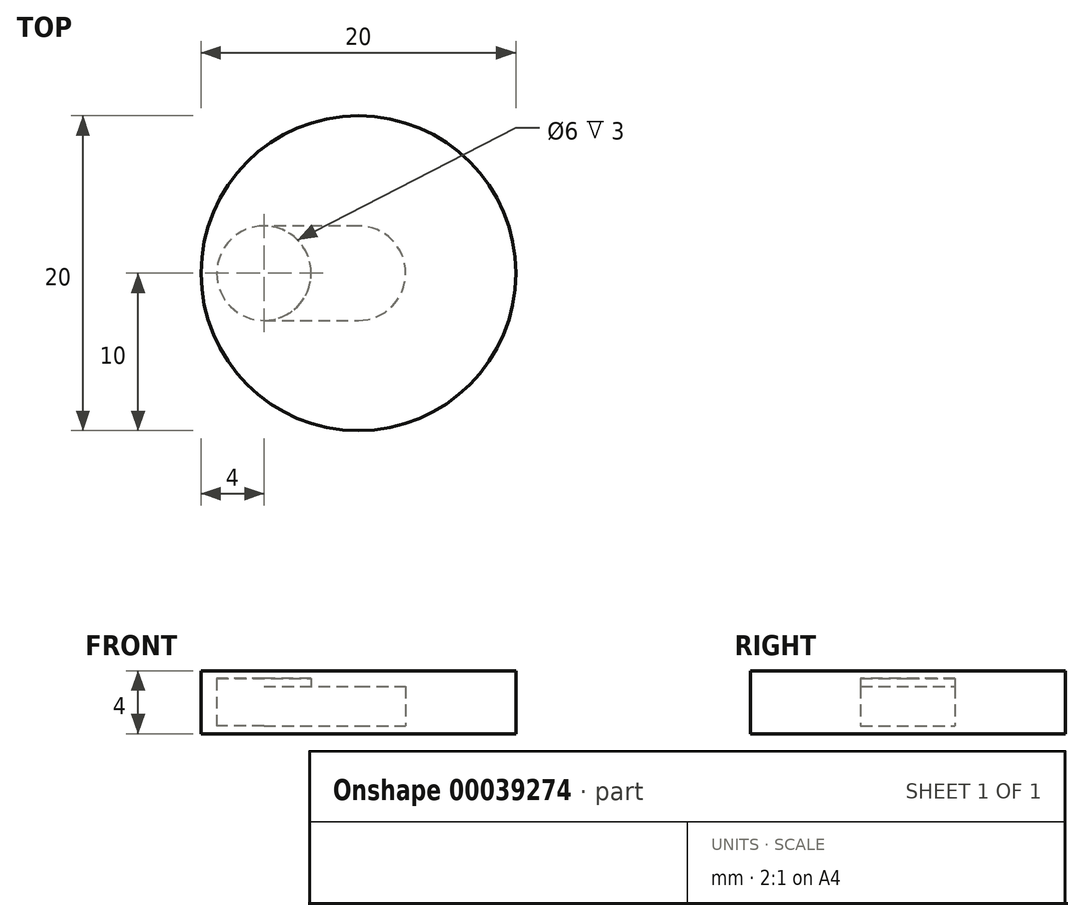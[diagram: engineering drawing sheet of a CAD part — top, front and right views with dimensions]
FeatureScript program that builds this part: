
annotation { "Feature Type Name" : "Feature", "Feature Type Description" : "" }
export const myFeature = defineFeature(function(context is Context, id is Id, definition is map)
    precondition{}
    {
        {
            var Q0;
            Q0=qCreatedBy(makeId("Top.planeOp"),FACE);
            var sketch = newSketch(context, id + "F0", { "sketchPlane" : qUnion([Q0])});
            skCircle(sketch, "E0", {"center": v(0, 0) * mm, "radius": 10 * mm});
            skCircle(sketch, "E1", {"center": v(0, 0) * mm, "radius": 3 * mm});
            skLineSegment(sketch, "E2", {"start": v(0, 0) * mm, "end": v(-6, 0) * mm, "construction": true});
            skCircle(sketch, "E3", {"center": v(-6, 0) * mm, "radius": 3 * mm});
            skLineSegment(sketch, "E4", {"start": v(-6, 0) * mm, "end": v(-6, 3) * mm, "construction": true});
            skLineSegment(sketch, "E5", {"start": v(-6, 3) * mm, "end": v(-6, 3) * mm});
            skLineSegment(sketch, "E6", {"start": v(0, 3) * mm, "end": v(0, 0) * mm, "construction": true});
            skLineSegment(sketch, "E7", {"start": v(0, 3) * mm, "end": v(-6, 3) * mm});
            skLineSegment(sketch, "E8", {"start": v(-6, 0) * mm, "end": v(-6, -3) * mm, "construction": true});
            skLineSegment(sketch, "E9", {"start": v(-6, -3) * mm, "end": v(-6, -3) * mm});
            skLineSegment(sketch, "E10", {"start": v(-6, -3) * mm, "end": v(0, -3) * mm});
            skLineSegment(sketch, "E11", {"start": v(0, 0) * mm, "end": v(0, -3) * mm, "construction": true});
            skSolve(sketch);
        }
        {
            var Q0;
            Q0 = qSketchRegion(id + "F0", true);
            var Q1;
            {var subQ0=sQuery(id+"F0.wireOp",EDGE,"E3");var subQ3=makeQuery(id+"F0.imprint","INTERSECT",VERTEX,{"derivedFrom":[subQ0,sQuery(id+"F0.wireOp",EDGE,"E7")]});Q1=makeQuery(id+"F0.imprint","IMPRINT",FACE,{"disambiguationData":[TD([[makeQuery(id+"F0.imprint","IMPRINT",EDGE,{"disambiguationData":[TD([[subQ3,1.0]])],"derivedFrom":subQ0}),1.0]])]});}
            var Q2;
            {var subQ0=sQuery(id+"F0.wireOp",EDGE,"E7");Q2=makeQuery(id+"F0.imprint","IMPRINT",FACE,{"disambiguationData":[TD([[makeQuery(id+"F0.imprint","IMPRINT",EDGE,{"derivedFrom":subQ0}),1.0]])]});}
            var Q3;
            {var subQ0=sQuery(id+"F0.wireOp",EDGE,"E10");Q3=makeQuery(id+"F0.imprint","IMPRINT",FACE,{"disambiguationData":[TD([[makeQuery(id+"F0.imprint","IMPRINT",EDGE,{"derivedFrom":subQ0}),1.0]])]});}
            var Q4;
            {var subQ0=sQuery(id+"F0.wireOp",EDGE,"E1");var subQ2=makeQuery(id+"F0.imprint","INTERSECT",VERTEX,{"derivedFrom":[subQ0,sQuery(id+"F0.wireOp",EDGE,"E7")]});Q4=makeQuery(id+"F0.imprint","IMPRINT",FACE,{"disambiguationData":[TD([[makeQuery(id+"F0.imprint","IMPRINT",EDGE,{"disambiguationData":[TD([[subQ2,-1.0]])],"derivedFrom":subQ0}),1.0]])]});}
            extrude(context, id + "F1", {"entities" : qUnion([Q0, Q1, Q2, Q3, Q4]), "depth" : 0.5 * mm});
        }
        {
            var Q0;
            Q0=makeQuery(id+"F0.imprint","IMPRINT",FACE,{"disambiguationData":[TD([[makeQuery(id+"F0.imprint","IMPRINT",EDGE,{"derivedFrom":sQuery(id+"F0.wireOp",EDGE,"E0")}),1.0]])]});
            extrude(context, id + "F2", {"entities" : qUnion([Q0]), "operationType" : NewBodyOperationType.ADD, "depth" : 3 * mm});
        }
        {
            var Q0;
            Q0=makeQuery(id+"F2.opExtrude","CAP_FACE",FACE,{"disambiguationData":[OSD([sQuery(id+"F0.wireOp",EDGE,"E0"),sQuery(id+"F0.wireOp",EDGE,"E1"),sQuery(id+"F0.wireOp",EDGE,"E3"),sQuery(id+"F0.wireOp",EDGE,"E7"),sQuery(id+"F0.wireOp",EDGE,"E10")])],"isStart":false});
            var sketch = newSketch(context, id + "F3", { "sketchPlane" : qUnion([Q0])});
            skCircle(sketch, "E12", {"center": v(0, 0) * mm, "radius": 10 * mm});
            skCircle(sketch, "E13", {"center": v(-6, 0) * mm, "radius": 3 * mm});
            skSolve(sketch);
        }
        {
            var Q0;
            Q0 = qSketchRegion(id + "F3", true);
            extrude(context, id + "F4", {"entities" : qUnion([Q0]), "operationType" : NewBodyOperationType.ADD, "depth" : 0.5 * mm});
        }
        {
            var Q0;
            Q0=makeQuery(id+"F4.opExtrude","CAP_FACE",FACE,{"disambiguationData":[OSD([sQuery(id+"F3.wireOp",EDGE,"E12"),sQuery(id+"F3.wireOp",EDGE,"E13")])],"isStart":false});
            var sketch = newSketch(context, id + "F5", { "sketchPlane" : qUnion([Q0])});
            skCircle(sketch, "E14", {"center": v(0, 0) * mm, "radius": 10 * mm});
            skSolve(sketch);
        }
        {
            var Q0;
            Q0 = qSketchRegion(id + "F5", true);
            extrude(context, id + "F6", {"entities" : qUnion([Q0]), "operationType" : NewBodyOperationType.ADD, "depth" : .5 * mm});
        }
    });
